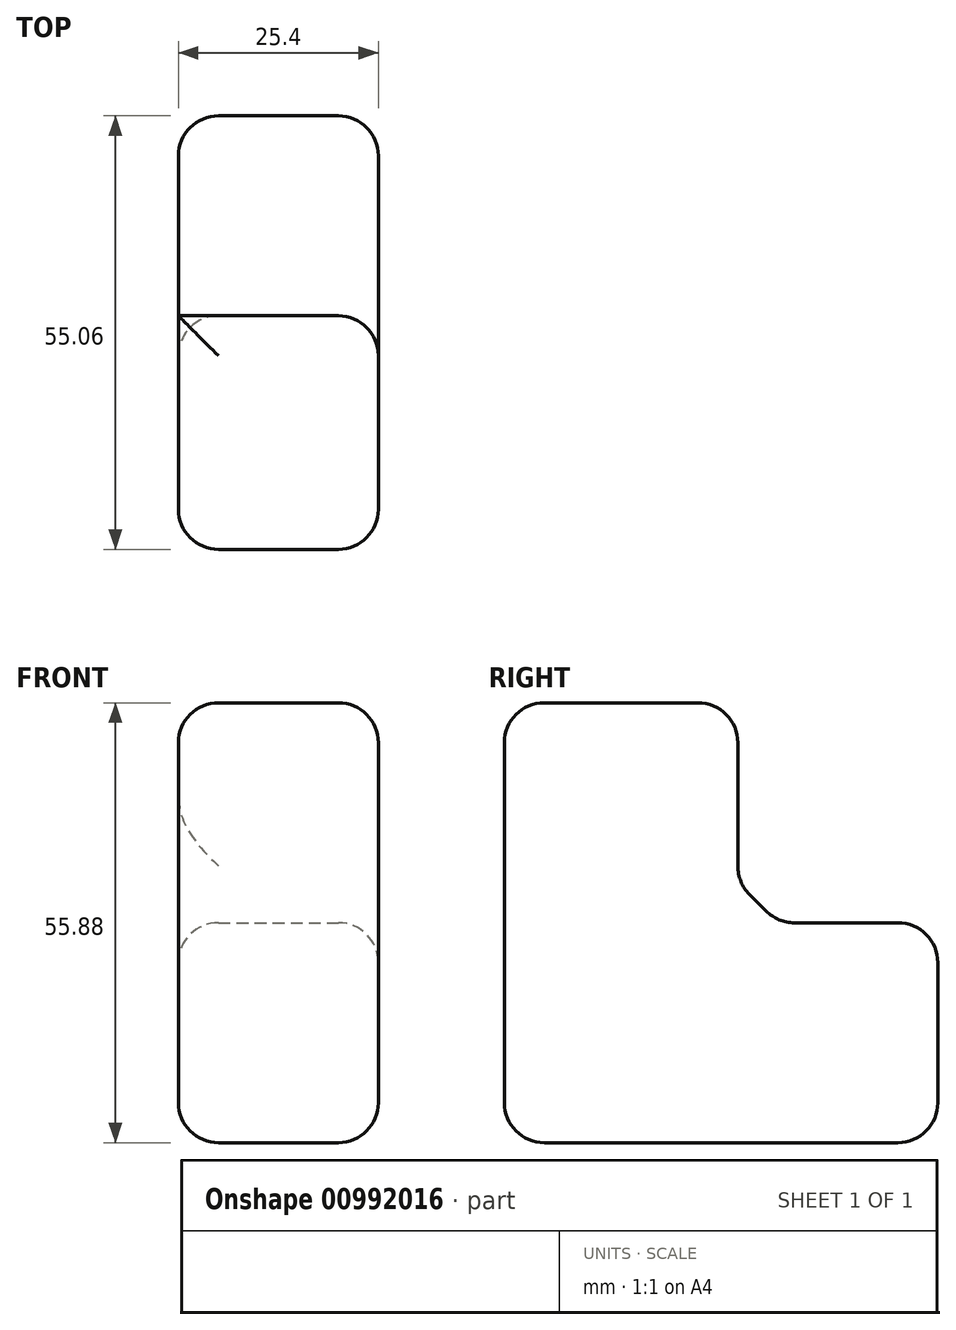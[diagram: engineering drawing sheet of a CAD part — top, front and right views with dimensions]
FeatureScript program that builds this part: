
annotation { "Feature Type Name" : "Feature", "Feature Type Description" : "" }
export const myFeature = defineFeature(function(context is Context, id is Id, definition is map)
    precondition{}
    {
        {
            var Q0;
            Q0=qCreatedBy(makeId("Right.planeOp"),FACE);
            var sketch = newSketch(context, id + "F0", { "sketchPlane" : qUnion([Q0])});
            skLineSegment(sketch, "E0.bottom", {"start": v(14.83, -27.94) * mm, "end": v(-14.83, -27.94) * mm});
            skLineSegment(sketch, "E0.top", {"start": v(14.83, 27.94) * mm, "end": v(-14.83, 27.94) * mm});
            skLineSegment(sketch, "E0.left", {"start": v(14.83, -27.94) * mm, "end": v(14.83, 27.94) * mm});
            skLineSegment(sketch, "E0.right", {"start": v(-14.83, -27.94) * mm, "end": v(-14.83, 27.94) * mm});
            skPoint(sketch, "E0.middle", {"position": v(0, 0) * mm});
            skLineSegment(sketch, "E1.bottom", {"start": v(14.83, 0) * mm, "end": v(40.23, 0) * mm});
            skLineSegment(sketch, "E1.top", {"start": v(14.83, -27.94) * mm, "end": v(40.23, -27.94) * mm});
            skLineSegment(sketch, "E1.left", {"start": v(14.83, 0) * mm, "end": v(14.83, -27.94) * mm});
            skLineSegment(sketch, "E1.right", {"start": v(40.23, 0) * mm, "end": v(40.23, -27.94) * mm});
            skSolve(sketch);
        }
        {
            var Q0;
            Q0 = qSketchRegion(id + "F0", true);
            extrude(context, id + "F1", {"entities" : qUnion([Q0]), "depth" : 25.4 * mm, "offsetDistance" : 25.4 * mm});
        }
        {
            var Q0;
            Q0=makeQuery(id+"F1.opExtrude","SWEPT_EDGE",EDGE,{"disambiguationData":[OSD([sQuery(id+"F0.wireOp",EDGE,"E0.left"),sQuery(id+"F0.wireOp",EDGE,"E1.bottom"),sQuery(id+"F0.wireOp",EDGE,"E1.left")])]});
            chamfer(context, id + "F2", {"entities" : qUnion([Q0]), "width" : 5.08 * mm, "tangentPropagation" : true});
        }
        {
            var Q0;
            Q0=makeQuery(id+"F1.opExtrude","SWEPT_EDGE",EDGE,{"disambiguationData":[OSD([sQuery(id+"F0.wireOp",EDGE,"E0.top"),sQuery(id+"F0.wireOp",EDGE,"E0.left")])]});
            var Q1;
            Q1=makeQuery(id+"F1.opExtrude","CAP_EDGE",EDGE,{"disambiguationData":[OSD([sQuery(id+"F0.wireOp",EDGE,"E0.left")])],"isStart":false});
            var Q2;
            Q2=makeQuery(id+"F1.opExtrude","CAP_EDGE",EDGE,{"disambiguationData":[OSD([sQuery(id+"F0.wireOp",EDGE,"E0.top")])],"isStart":false});
            var Q3;
            Q3=makeQuery(id+"F1.opExtrude","SWEPT_EDGE",EDGE,{"disambiguationData":[OSD([sQuery(id+"F0.wireOp",EDGE,"E0.top"),sQuery(id+"F0.wireOp",EDGE,"E0.right")])]});
            var Q4;
            Q4=makeQuery(id+"F1.opExtrude","CAP_EDGE",EDGE,{"disambiguationData":[OSD([sQuery(id+"F0.wireOp",EDGE,"E0.top")])],"isStart":true});
            var Q5;
            Q5=makeQuery(id+"F1.opExtrude","CAP_EDGE",EDGE,{"disambiguationData":[OSD([sQuery(id+"F0.wireOp",EDGE,"E0.right")])],"isStart":false});
            var Q6;
            Q6=makeQuery(id+"F1.opExtrude","CAP_EDGE",EDGE,{"disambiguationData":[OSD([sQuery(id+"F0.wireOp",EDGE,"E0.bottom"),sQuery(id+"F0.wireOp",EDGE,"E1.top")])],"isStart":false});
            var Q7;
            Q7=makeQuery(id+"F1.opExtrude","CAP_EDGE",EDGE,{"disambiguationData":[OSD([sQuery(id+"F0.wireOp",EDGE,"E1.bottom")])],"isStart":false});
            var Q8;
            Q8=makeQuery(id+"F1.opExtrude","CAP_EDGE",EDGE,{"disambiguationData":[OSD([sQuery(id+"F0.wireOp",EDGE,"E1.right")])],"isStart":false});
            var Q9;
            Q9=makeQuery(id+"F1.opExtrude","SWEPT_EDGE",EDGE,{"disambiguationData":[OSD([sQuery(id+"F0.wireOp",EDGE,"E1.bottom"),sQuery(id+"F0.wireOp",EDGE,"E1.right")])]});
            var Q10;
            Q10=makeQuery(id+"F1.opExtrude","CAP_EDGE",EDGE,{"disambiguationData":[OSD([sQuery(id+"F0.wireOp",EDGE,"E1.bottom")])],"isStart":true});
            var Q11;
            Q11=makeQuery(id+"F1.opExtrude","CAP_EDGE",EDGE,{"disambiguationData":[OSD([sQuery(id+"F0.wireOp",EDGE,"E1.right")])],"isStart":true});
            var Q12;
            Q12=makeQuery(id+"F1.opExtrude","SWEPT_EDGE",EDGE,{"disambiguationData":[OSD([sQuery(id+"F0.wireOp",EDGE,"E1.top"),sQuery(id+"F0.wireOp",EDGE,"E1.right")])]});
            var Q13;
            {var subQ0=sQuery(id+"F0.wireOp",EDGE,"E0.left");Q13=makeQuery(id+"F2.opChamfer","BLEND_EDGE",EDGE,{"blendedFrom":[makeQuery(id+"F1.opExtrude","SWEPT_EDGE",EDGE,{"disambiguationData":[OSD([subQ0,sQuery(id+"F0.wireOp",EDGE,"E1.bottom"),sQuery(id+"F0.wireOp",EDGE,"E1.left")])]}),makeQuery(id+"F1.opExtrude","SWEPT_FACE",FACE,{"disambiguationData":[OSD([subQ0])]})],"blendedInto":[makeQuery(id+"F1.opExtrude","SWEPT_FACE",FACE,{"disambiguationData":[OSD([subQ0])]})]});}
            var Q14;
            {var subQ0=sQuery(id+"F0.wireOp",EDGE,"E1.bottom");Q14=makeQuery(id+"F2.opChamfer","BLEND_EDGE",EDGE,{"blendedFrom":[makeQuery(id+"F1.opExtrude","SWEPT_EDGE",EDGE,{"disambiguationData":[OSD([sQuery(id+"F0.wireOp",EDGE,"E0.left"),subQ0,sQuery(id+"F0.wireOp",EDGE,"E1.left")])]}),makeQuery(id+"F1.opExtrude","SWEPT_FACE",FACE,{"disambiguationData":[OSD([subQ0])]})],"blendedInto":[makeQuery(id+"F1.opExtrude","SWEPT_FACE",FACE,{"disambiguationData":[OSD([subQ0])]})]});}
            var Q15;
            {var subQ0=sQuery(id+"F0.wireOp",EDGE,"E1.bottom");var subQ1=sQuery(id+"F0.wireOp",EDGE,"E0.left");Q15=makeQuery(id+"F2.opChamfer","BLEND_EDGE",EDGE,{"blendedFrom":[makeQuery(id+"F1.opExtrude","SWEPT_EDGE",EDGE,{"disambiguationData":[OSD([subQ1,subQ0,sQuery(id+"F0.wireOp",EDGE,"E1.left")])]}),makeQuery(id+"F1.opExtrude","CAP_FACE",FACE,{"disambiguationData":[OSD([sQuery(id+"F0.wireOp",EDGE,"E0.bottom"),sQuery(id+"F0.wireOp",EDGE,"E0.top"),subQ1,sQuery(id+"F0.wireOp",EDGE,"E0.right"),subQ0,sQuery(id+"F0.wireOp",EDGE,"E1.top"),sQuery(id+"F0.wireOp",EDGE,"E1.right")])],"isStart":true})],"blendedInto":[makeQuery(id+"F1.opExtrude","CAP_FACE",FACE,{"disambiguationData":[OSD([sQuery(id+"F0.wireOp",EDGE,"E0.bottom"),sQuery(id+"F0.wireOp",EDGE,"E0.top"),subQ1,sQuery(id+"F0.wireOp",EDGE,"E0.right"),subQ0,sQuery(id+"F0.wireOp",EDGE,"E1.top"),sQuery(id+"F0.wireOp",EDGE,"E1.right")])],"isStart":true})]});}
            var Q16;
            {var subQ0=sQuery(id+"F0.wireOp",EDGE,"E1.bottom");var subQ1=sQuery(id+"F0.wireOp",EDGE,"E0.left");Q16=makeQuery(id+"F2.opChamfer","BLEND_EDGE",EDGE,{"blendedFrom":[makeQuery(id+"F1.opExtrude","SWEPT_EDGE",EDGE,{"disambiguationData":[OSD([subQ1,subQ0,sQuery(id+"F0.wireOp",EDGE,"E1.left")])]}),makeQuery(id+"F1.opExtrude","CAP_FACE",FACE,{"disambiguationData":[OSD([sQuery(id+"F0.wireOp",EDGE,"E0.bottom"),sQuery(id+"F0.wireOp",EDGE,"E0.top"),subQ1,sQuery(id+"F0.wireOp",EDGE,"E0.right"),subQ0,sQuery(id+"F0.wireOp",EDGE,"E1.top"),sQuery(id+"F0.wireOp",EDGE,"E1.right")])],"isStart":false})],"blendedInto":[makeQuery(id+"F1.opExtrude","CAP_FACE",FACE,{"disambiguationData":[OSD([sQuery(id+"F0.wireOp",EDGE,"E0.bottom"),sQuery(id+"F0.wireOp",EDGE,"E0.top"),subQ1,sQuery(id+"F0.wireOp",EDGE,"E0.right"),subQ0,sQuery(id+"F0.wireOp",EDGE,"E1.top"),sQuery(id+"F0.wireOp",EDGE,"E1.right")])],"isStart":false})]});}
            var Q17;
            Q17=makeQuery(id+"F1.opExtrude","CAP_EDGE",EDGE,{"disambiguationData":[OSD([sQuery(id+"F0.wireOp",EDGE,"E0.bottom"),sQuery(id+"F0.wireOp",EDGE,"E1.top")])],"isStart":true});
            var Q18;
            Q18=makeQuery(id+"F1.opExtrude","CAP_EDGE",EDGE,{"disambiguationData":[OSD([sQuery(id+"F0.wireOp",EDGE,"E0.right")])],"isStart":true});
            var Q19;
            Q19=makeQuery(id+"F1.opExtrude","SWEPT_EDGE",EDGE,{"disambiguationData":[OSD([sQuery(id+"F0.wireOp",EDGE,"E0.bottom"),sQuery(id+"F0.wireOp",EDGE,"E0.right")])]});
            fillet(context, id + "F3", {"entities" : qUnion([Q0, Q1, Q2, Q3, Q4, Q5, Q6, Q7, Q8, Q9, Q10, Q11, Q12, Q13, Q14, Q15, Q16, Q17, Q18, Q19]), "radius" : 5.08 * mm, "tangentPropagation" : true, "allowEdgeOverflow" : false});
        }
    });
